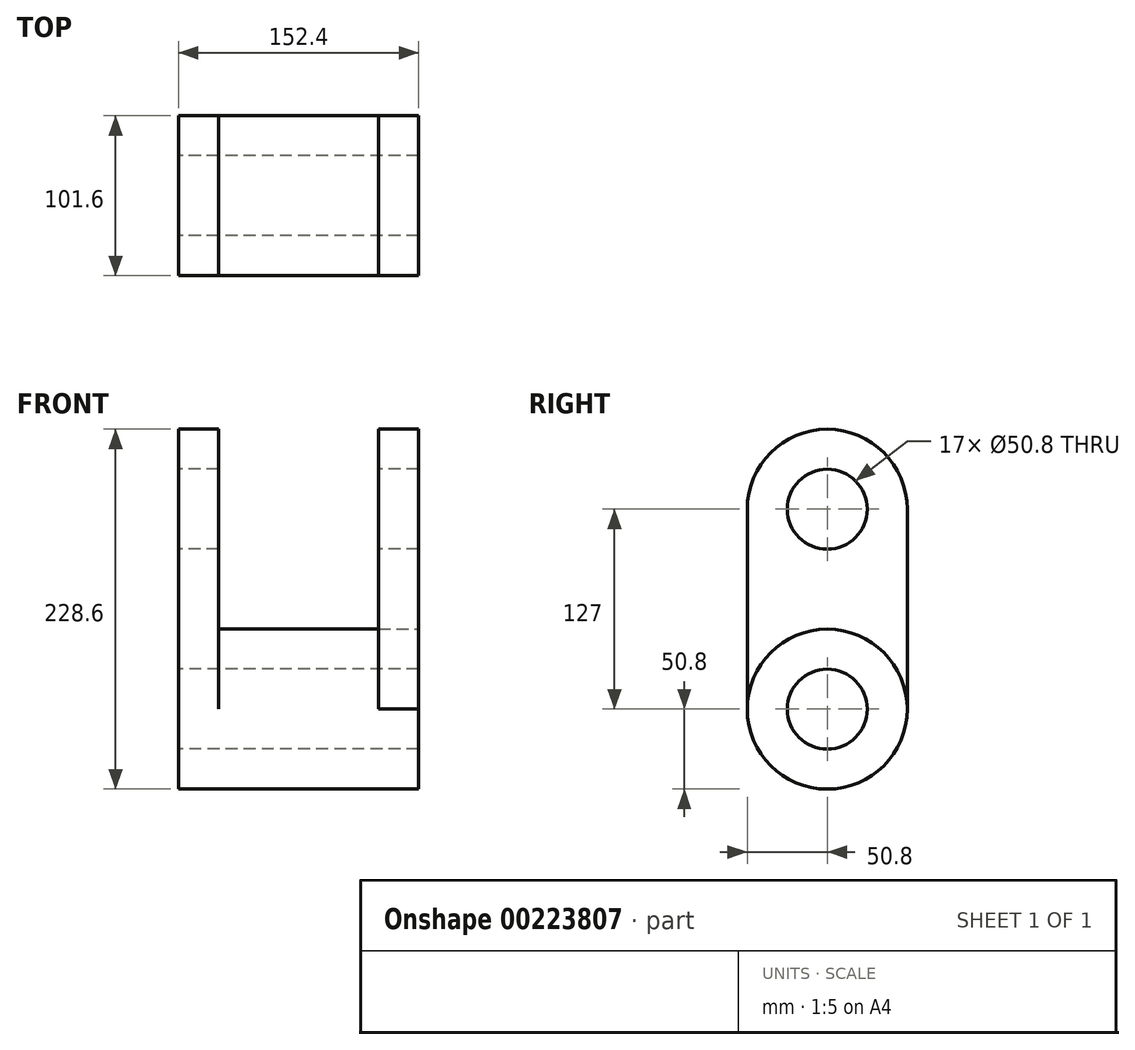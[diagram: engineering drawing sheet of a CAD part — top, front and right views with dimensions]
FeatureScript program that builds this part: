
annotation { "Feature Type Name" : "Feature", "Feature Type Description" : "" }
export const myFeature = defineFeature(function(context is Context, id is Id, definition is map)
    precondition{}
    {
        {
            var Q0;
            Q0=qCreatedBy(makeId("Right.planeOp"),FACE);
            var sketch = newSketch(context, id + "F0", { "sketchPlane" : qUnion([Q0])});
            skCircle(sketch, "E0", {"center": v(0, 0) * mm, "radius": 50.8 * mm});
            skSolve(sketch);
        }
        {
            var Q0;
            Q0=makeQuery(id+"F0.imprint","IMPRINT",FACE,{"disambiguationData":[TD([[makeQuery(id+"F0.imprint","IMPRINT",EDGE,{"derivedFrom":sQuery(id+"F0.wireOp",EDGE,"E0")}),1.0]])]});
            extrude(context, id + "F1", {"entities" : qUnion([Q0]), "depth" : 152.4 * mm});
        }
        {
            var Q0;
            Q0=makeQuery(id+"F1.opExtrude","CAP_FACE",FACE,{"disambiguationData":[OSD([sQuery(id+"F0.wireOp",EDGE,"E0")])],"isStart":false});
            var sketch = newSketch(context, id + "F2", { "sketchPlane" : qUnion([Q0])});
            skLineSegment(sketch, "E1", {"start": v(-50.8, 0) * mm, "end": v(-50.8, 127) * mm});
            skLineSegment(sketch, "E2", {"start": v(50.8, 0) * mm, "end": v(50.8, 127) * mm});
            skLineSegment(sketch, "E3", {"start": v(0, 162.71) * mm, "end": v(0, -31.53) * mm, "construction": true});
            skArc(sketch, "E4", {"start": v(50.8, 127) * mm, "mid": v(0, 177.8) * mm, "end": v(-50.8, 127) * mm});
            skLineSegment(sketch, "E5", {"start": v(-50.8, 0) * mm, "end": v(50.8, 0) * mm});
            skSolve(sketch);
        }
        {
            var Q0;
            {var subQ0=sQuery(id+"F2.wireOp",EDGE,"E1");Q0=makeQuery(id+"F2.imprint","IMPRINT",FACE,{"disambiguationData":[TD([[makeQuery(id+"F2.imprint","IMPRINT",EDGE,{"derivedFrom":subQ0}),-1.0]])]});}
            extrude(context, id + "F3", {"entities" : qUnion([Q0]), "oppositeDirection" : true, "depth" : 25.4 * mm});
        }
        {
            var Q0;
            Q0=makeQuery(id+"F1.opExtrude","CAP_FACE",FACE,{"disambiguationData":[OSD([sQuery(id+"F0.wireOp",EDGE,"E0")])],"isStart":true});
            var sketch = newSketch(context, id + "F4", { "sketchPlane" : qUnion([Q0])});
            skLineSegment(sketch, "E6", {"start": v(-50.8, 0) * mm, "end": v(-50.8, 127) * mm});
            skLineSegment(sketch, "E7", {"start": v(50.8, 0) * mm, "end": v(50.8, 127) * mm});
            skArc(sketch, "E8", {"start": v(50.8, 127) * mm, "mid": v(0, 177.8) * mm, "end": v(-50.8, 127) * mm});
            skLineSegment(sketch, "E9", {"start": v(-50.8, 0) * mm, "end": v(50.8, 0) * mm});
            skSolve(sketch);
        }
        {
            var Q0;
            Q0 = qSketchRegion(id + "F4", true);
            extrude(context, id + "F5", {"entities" : qUnion([Q0]), "operationType" : NewBodyOperationType.ADD, "oppositeDirection" : true, "depth" : 25.4 * mm});
        }
        {
            var Q0;
            Q0=makeQuery(id+"F5.boolean.opBoolean","MERGE",FACE,{"derivedFrom":[makeQuery(id+"F1.opExtrude","CAP_FACE",FACE,{"disambiguationData":[OSD([sQuery(id+"F0.wireOp",EDGE,"E0")])],"isStart":true}),makeQuery(id+"F5.opExtrude","CAP_FACE",FACE,{"disambiguationData":[OSD([sQuery(id+"F4.wireOp",EDGE,"E6"),sQuery(id+"F4.wireOp",EDGE,"E7"),sQuery(id+"F4.wireOp",EDGE,"E8"),sQuery(id+"F4.wireOp",EDGE,"E9")])],"isStart":true})]});
            var sketch = newSketch(context, id + "F6", { "sketchPlane" : qUnion([Q0])});
            skLineSegment(sketch, "E10", {"start": v(0, 0) * mm, "end": v(0, 196.11) * mm, "construction": true});
            skLineSegment(sketch, "E11", {"start": v(0, 127) * mm, "end": v(-88.11, 127) * mm, "construction": true});
            skLineSegment(sketch, "E12", {"start": v(-88.11, 127) * mm, "end": v(81.47, 127) * mm, "construction": true});
            skCircle(sketch, "E13", {"center": v(0, 127) * mm, "radius": 25.4 * mm});
            skCircle(sketch, "E14", {"center": v(0, 0) * mm, "radius": 25.4 * mm});
            skSolve(sketch);
        }
        {
            var Q0;
            Q0 = qSketchRegion(id + "F6", true);
            extrude(context, id + "F7", {"entities" : qUnion([Q0]), "operationType" : NewBodyOperationType.REMOVE, "endBound" : BoundingType.THROUGH_ALL, "oppositeDirection" : true, "depth" : 25.4 * mm});
        }
        {
            var Q0;
            Q0=makeQuery(id+"F3.opExtrude","CAP_FACE",FACE,{"disambiguationData":[OSD([sQuery(id+"F0.wireOp",EDGE,"E0"),sQuery(id+"F2.wireOp",EDGE,"E1"),sQuery(id+"F2.wireOp",EDGE,"E2"),sQuery(id+"F2.wireOp",EDGE,"E4")])],"isStart":true});
            var sketch = newSketch(context, id + "F8", { "sketchPlane" : qUnion([Q0])});
            skLineSegment(sketch, "E15", {"start": v(0, -30.43) * mm, "end": v(0, 209.56) * mm, "construction": true});
            skLineSegment(sketch, "E16", {"start": v(0, 127) * mm, "end": v(-88.55, 127) * mm, "construction": true});
            skLineSegment(sketch, "E17", {"start": v(-88.55, 127) * mm, "end": v(75.71, 127) * mm, "construction": true});
            skCircle(sketch, "E18", {"center": v(0, 127) * mm, "radius": 25.4 * mm});
            skSolve(sketch);
        }
        {
            var Q0;
            Q0 = qSketchRegion(id + "F8", true);
            extrude(context, id + "F9", {"entities" : qUnion([Q0]), "operationType" : NewBodyOperationType.REMOVE, "endBound" : BoundingType.THROUGH_ALL, "oppositeDirection" : true, "depth" : 25.4 * mm});
        }
    });
